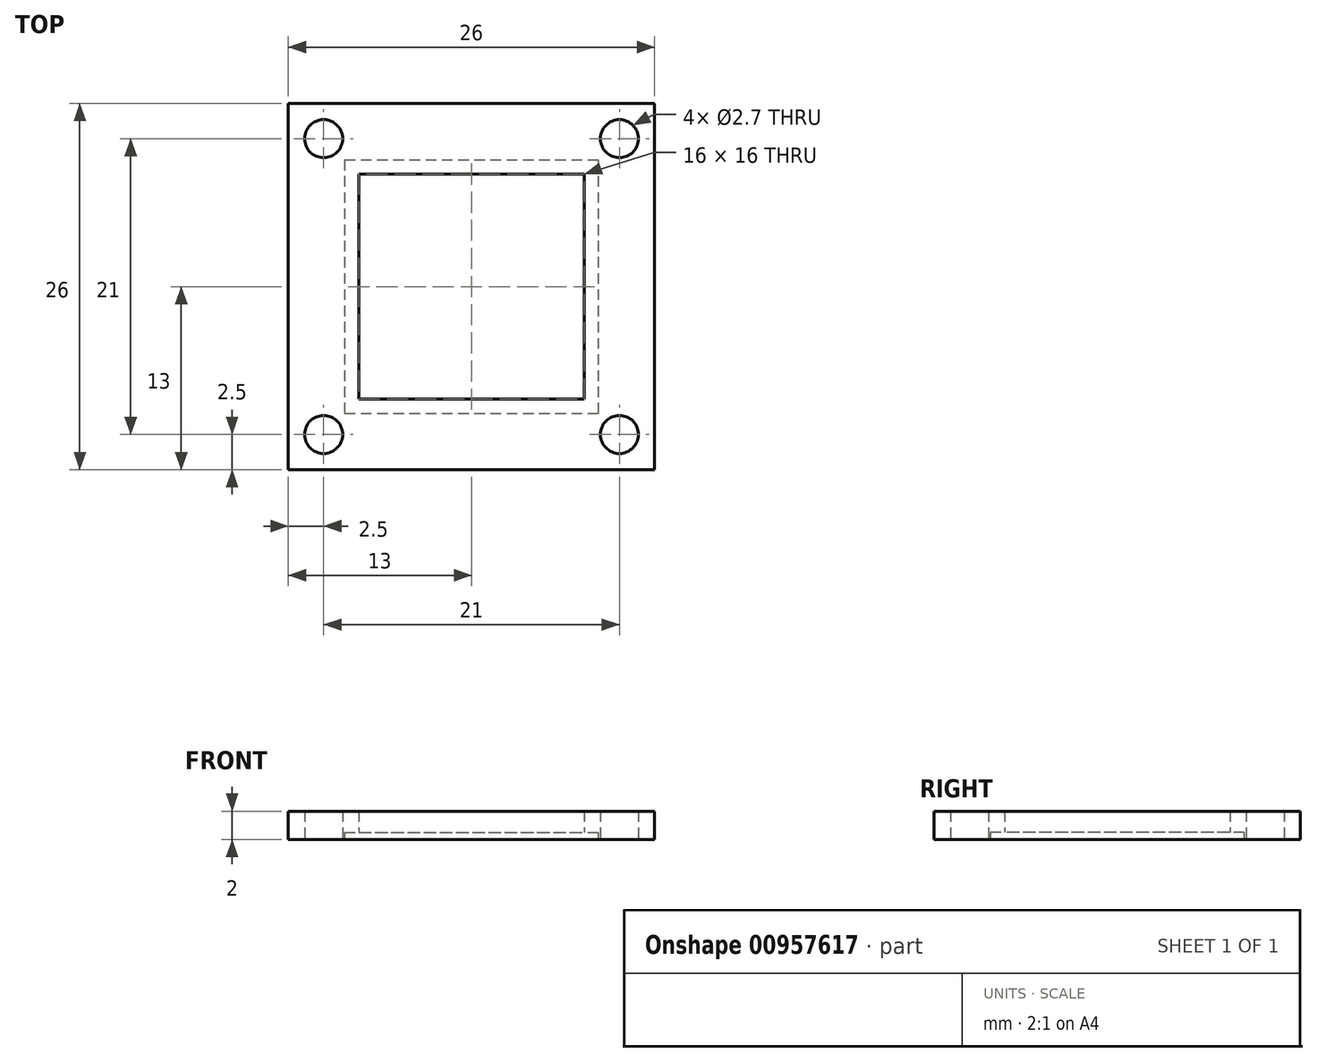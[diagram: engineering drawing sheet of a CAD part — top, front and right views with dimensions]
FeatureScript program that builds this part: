
annotation { "Feature Type Name" : "Feature", "Feature Type Description" : "" }
export const myFeature = defineFeature(function(context is Context, id is Id, definition is map)
    precondition{}
    {
        {
            var Q0;
            Q0=qCreatedBy(makeId("Top.planeOp"),FACE);
            var sketch = newSketch(context, id + "F0", { "sketchPlane" : qUnion([Q0])});
            skLineSegment(sketch, "E0.bottom", {"start": v(-13, 13) * mm, "end": v(13, 13) * mm});
            skLineSegment(sketch, "E0.top", {"start": v(-13, -13) * mm, "end": v(13, -13) * mm});
            skLineSegment(sketch, "E0.left", {"start": v(-13, 13) * mm, "end": v(-13, -13) * mm});
            skLineSegment(sketch, "E0.right", {"start": v(13, 13) * mm, "end": v(13, -13) * mm});
            skPoint(sketch, "E0.middle", {"position": v(0, 0) * mm});
            skLineSegment(sketch, "E1.bottom", {"start": v(-8, 8) * mm, "end": v(8, 8) * mm});
            skLineSegment(sketch, "E1.top", {"start": v(-8, -8) * mm, "end": v(8, -8) * mm});
            skLineSegment(sketch, "E1.left", {"start": v(-8, 8) * mm, "end": v(-8, -8) * mm});
            skLineSegment(sketch, "E1.right", {"start": v(8, 8) * mm, "end": v(8, -8) * mm});
            skLineSegment(sketch, "E2.bottom", {"start": v(-9, 9) * mm, "end": v(9, 9) * mm});
            skLineSegment(sketch, "E2.top", {"start": v(-9, -9) * mm, "end": v(9, -9) * mm});
            skLineSegment(sketch, "E2.left", {"start": v(-9, 9) * mm, "end": v(-9, -9) * mm});
            skLineSegment(sketch, "E2.right", {"start": v(9, 9) * mm, "end": v(9, -9) * mm});
            skSolve(sketch);
        }
        {
            var Q0;
            Q0=makeQuery(id+"F0.imprint","IMPRINT",FACE,{"disambiguationData":[TD([[makeQuery(id+"F0.imprint","IMPRINT",EDGE,{"derivedFrom":sQuery(id+"F0.wireOp",EDGE,"E0.bottom")}),-1.0]])]});
            var Q1;
            Q1=makeQuery(id+"F0.imprint","IMPRINT",FACE,{"disambiguationData":[TD([[makeQuery(id+"F0.imprint","IMPRINT",EDGE,{"derivedFrom":sQuery(id+"F0.wireOp",EDGE,"E1.bottom")}),1.0]])]});
            extrude(context, id + "F1", {"entities" : qUnion([Q0, Q1]), "depth" : 2 * mm, "offsetDistance" : 25 * mm});
        }
        {
            var Q0;
            Q0=makeQuery(id+"F0.imprint","IMPRINT",FACE,{"disambiguationData":[TD([[makeQuery(id+"F0.imprint","IMPRINT",EDGE,{"derivedFrom":sQuery(id+"F0.wireOp",EDGE,"E1.bottom")}),1.0]])]});
            extrude(context, id + "F2", {"entities" : qUnion([Q0]), "operationType" : NewBodyOperationType.REMOVE, "depth" : 0.5 * mm, "offsetDistance" : 25 * mm});
        }
        {
            var Q0;
            Q0=makeQuery(id+"F1.opExtrude","CAP_FACE",FACE,{"disambiguationData":[OSD([sQuery(id+"F0.wireOp",EDGE,"E0.bottom"),sQuery(id+"F0.wireOp",EDGE,"E0.top"),sQuery(id+"F0.wireOp",EDGE,"E0.left"),sQuery(id+"F0.wireOp",EDGE,"E0.right"),sQuery(id+"F0.wireOp",EDGE,"E1.bottom"),sQuery(id+"F0.wireOp",EDGE,"E1.top"),sQuery(id+"F0.wireOp",EDGE,"E1.left"),sQuery(id+"F0.wireOp",EDGE,"E1.right")])],"isStart":true});
            var sketch = newSketch(context, id + "F3", { "sketchPlane" : qUnion([Q0])});
            skLineSegment(sketch, "E3", {"start": v(-13, 13) * mm, "end": v(-9, 9) * mm, "construction": true});
            skPoint(sketch, "E4", {"position": v(-10.5, 10.5) * mm});
            skPoint(sketch, "E5.MirrorP", {"position": v(10.5, 10.5) * mm});
            skLineSegment(sketch, "E6.MirrorCS", {"start": v(13, 13) * mm, "end": v(9, 9) * mm, "construction": true});
            skLineSegment(sketch, "E7.MirrorCS", {"start": v(-13, -13) * mm, "end": v(-9, -9) * mm, "construction": true});
            skPoint(sketch, "E8.MirrorP", {"position": v(-10.5, -10.5) * mm});
            skLineSegment(sketch, "E9.MirrorCS", {"start": v(13, -13) * mm, "end": v(9, -9) * mm, "construction": true});
            skPoint(sketch, "E10.MirrorP", {"position": v(10.5, -10.5) * mm});
            skSolve(sketch);
        }
        {
            var Q0;
            Q0=sQuery(id+"F3.wireOp",VERTEX,"E4");
            var Q1;
            Q1=sQuery(id+"F3.wireOp",VERTEX,"E5.MirrorP");
            var Q2;
            Q2=sQuery(id+"F3.wireOp",VERTEX,"E10.MirrorP");
            var Q3;
            Q3=sQuery(id+"F3.wireOp",VERTEX,"E8.MirrorP");
            var Q4;
            Q4=makeQuery(id+"F1.opExtrude","SWEPT_BODY",BODY,{"disambiguationData":[OSD([sQuery(id+"F0.wireOp",EDGE,"E0.bottom"),sQuery(id+"F0.wireOp",EDGE,"E0.top"),sQuery(id+"F0.wireOp",EDGE,"E0.left"),sQuery(id+"F0.wireOp",EDGE,"E0.right"),sQuery(id+"F0.wireOp",EDGE,"E1.bottom"),sQuery(id+"F0.wireOp",EDGE,"E1.top"),sQuery(id+"F0.wireOp",EDGE,"E1.left"),sQuery(id+"F0.wireOp",EDGE,"E1.right")])]});
            hole(context, id + "F4", {"style" : HoleStyle.SIMPLE, "endStyle" : HoleEndStyle.BLIND, "standardTappedOrClearance" : lookupTablePath({ "standard" : "ISO", "engagement" : "50%", "pitch" : "0.5 mm", "size" : "M3", "type" : "Tapped" }), "standardBlindInLast" : lookupTablePath({ "standard" : "ISO", "fit" : "Normal", "engagement" : "50%", "pitch" : "0.5 mm", "size" : "M3", "type" : "Clearance & tapped" }), "holeDiameter" : 2.7 * mm, "majorDiameter" : 3 * mm, "showTappedDepth" : true, "holeDepth" : 3.5 * mm, "isTappedThrough" : true, "tappedDepth" : 2 * mm, "tapClearance" : 3, "locations" : qUnion([Q0, Q1, Q2, Q3]), "scope" : qUnion([Q4])});
        }
    });
